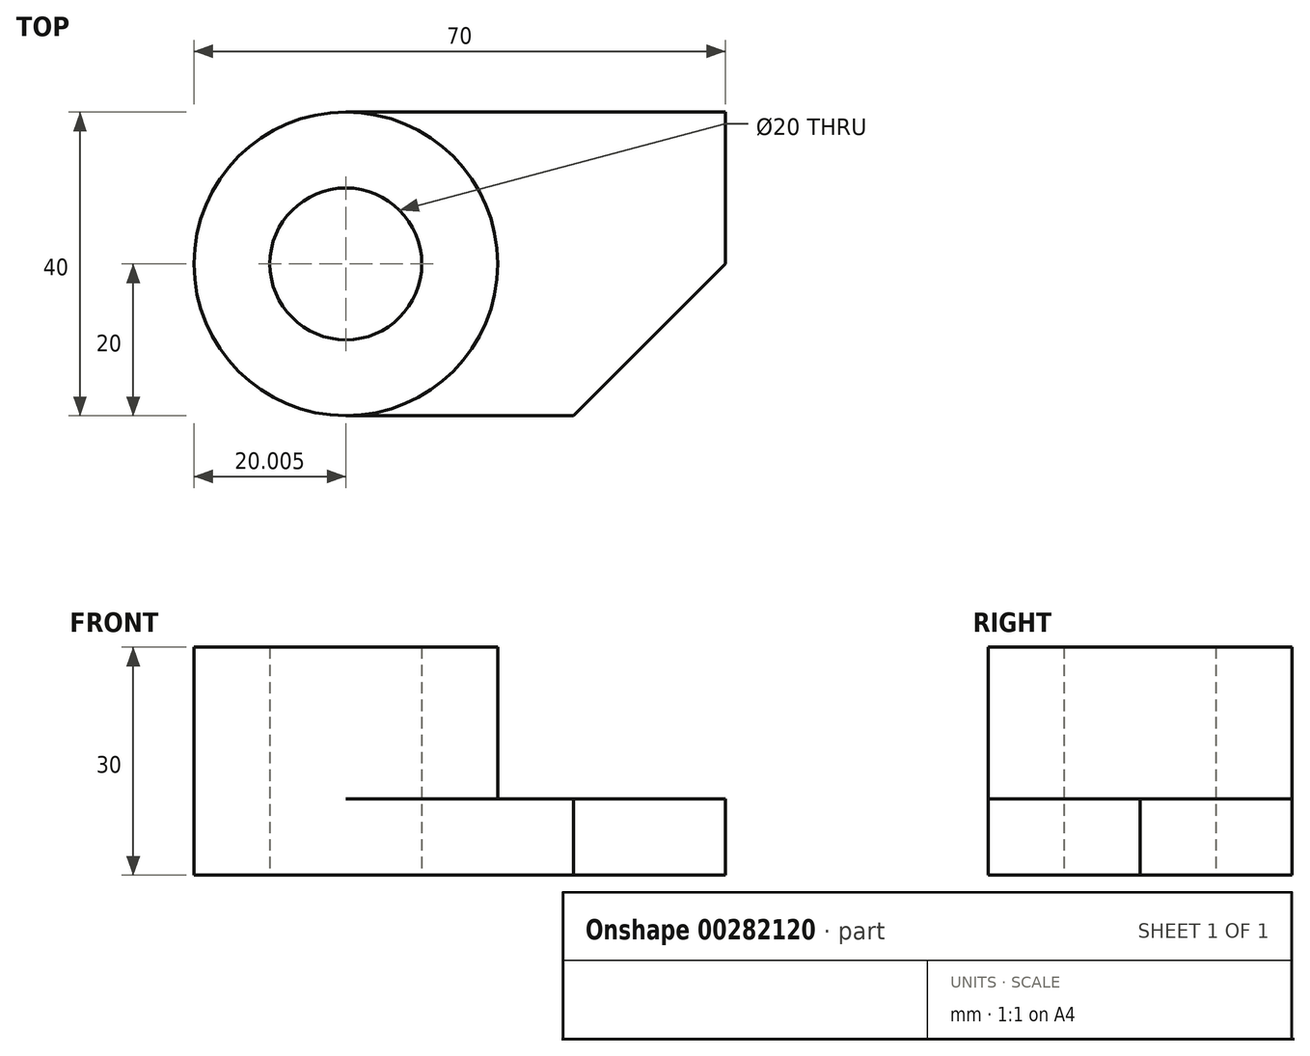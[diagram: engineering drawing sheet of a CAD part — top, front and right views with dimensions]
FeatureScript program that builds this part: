
annotation { "Feature Type Name" : "Feature", "Feature Type Description" : "" }
export const myFeature = defineFeature(function(context is Context, id is Id, definition is map)
    precondition{}
    {
        {
            var Q0;
            Q0=qCreatedBy(makeId("Top.planeOp"),FACE);
            var sketch = newSketch(context, id + "F0", { "sketchPlane" : qUnion([Q0])});
            skLineSegment(sketch, "E0", {"start": v(37.91, 20) * mm, "end": v(37.91, 40) * mm});
            skLineSegment(sketch, "E1", {"start": v(37.91, 40) * mm, "end": v(-12.09, 40) * mm});
            skLineSegment(sketch, "E2", {"start": v(-12.09, 0) * mm, "end": v(17.91, 0) * mm});
            skLineSegment(sketch, "E3", {"start": v(37.91, 20) * mm, "end": v(17.91, 0) * mm});
            skPoint(sketch, "E4.orphan", {"position": v(37.91, 0) * mm});
            skCircle(sketch, "E5", {"center": v(-12.09, 20) * mm, "radius": 10 * mm});
            skArc(sketch, "E6", {"start": v(-12.09, 40) * mm, "mid": v(-32.09, 20) * mm, "end": v(-12.09, 0) * mm});
            skPoint(sketch, "E7.orphan", {"position": v(-32.09, 0) * mm});
            skSolve(sketch);
        }
        {
            var Q0;
            Q0 = qSketchRegion(id + "F0", true);
            extrude(context, id + "F1", {"entities" : qUnion([Q0]), "depth" : 10 * mm});
        }
        {
            var Q0;
            Q0=makeQuery(id+"F1.opExtrude","CAP_FACE",FACE,{"disambiguationData":[OSD([sQuery(id+"F0.wireOp",EDGE,"E0"),sQuery(id+"F0.wireOp",EDGE,"E1"),sQuery(id+"F0.wireOp",EDGE,"E2"),sQuery(id+"F0.wireOp",EDGE,"E3"),sQuery(id+"F0.wireOp",EDGE,"E5"),sQuery(id+"F0.wireOp",EDGE,"E6")])],"isStart":false});
            var sketch = newSketch(context, id + "F2", { "sketchPlane" : qUnion([Q0])});
            skCircle(sketch, "E8", {"center": v(-12.09, 20) * mm, "radius": 20 * mm});
            skCircle(sketch, "E9", {"center": v(-12.09, 20) * mm, "radius": 10 * mm});
            skSolve(sketch);
        }
        {
            var Q0;
            Q0 = qSketchRegion(id + "F2", true);
            extrude(context, id + "F3", {"entities" : qUnion([Q0]), "operationType" : NewBodyOperationType.ADD, "depth" : 20 * mm});
        }
    });
